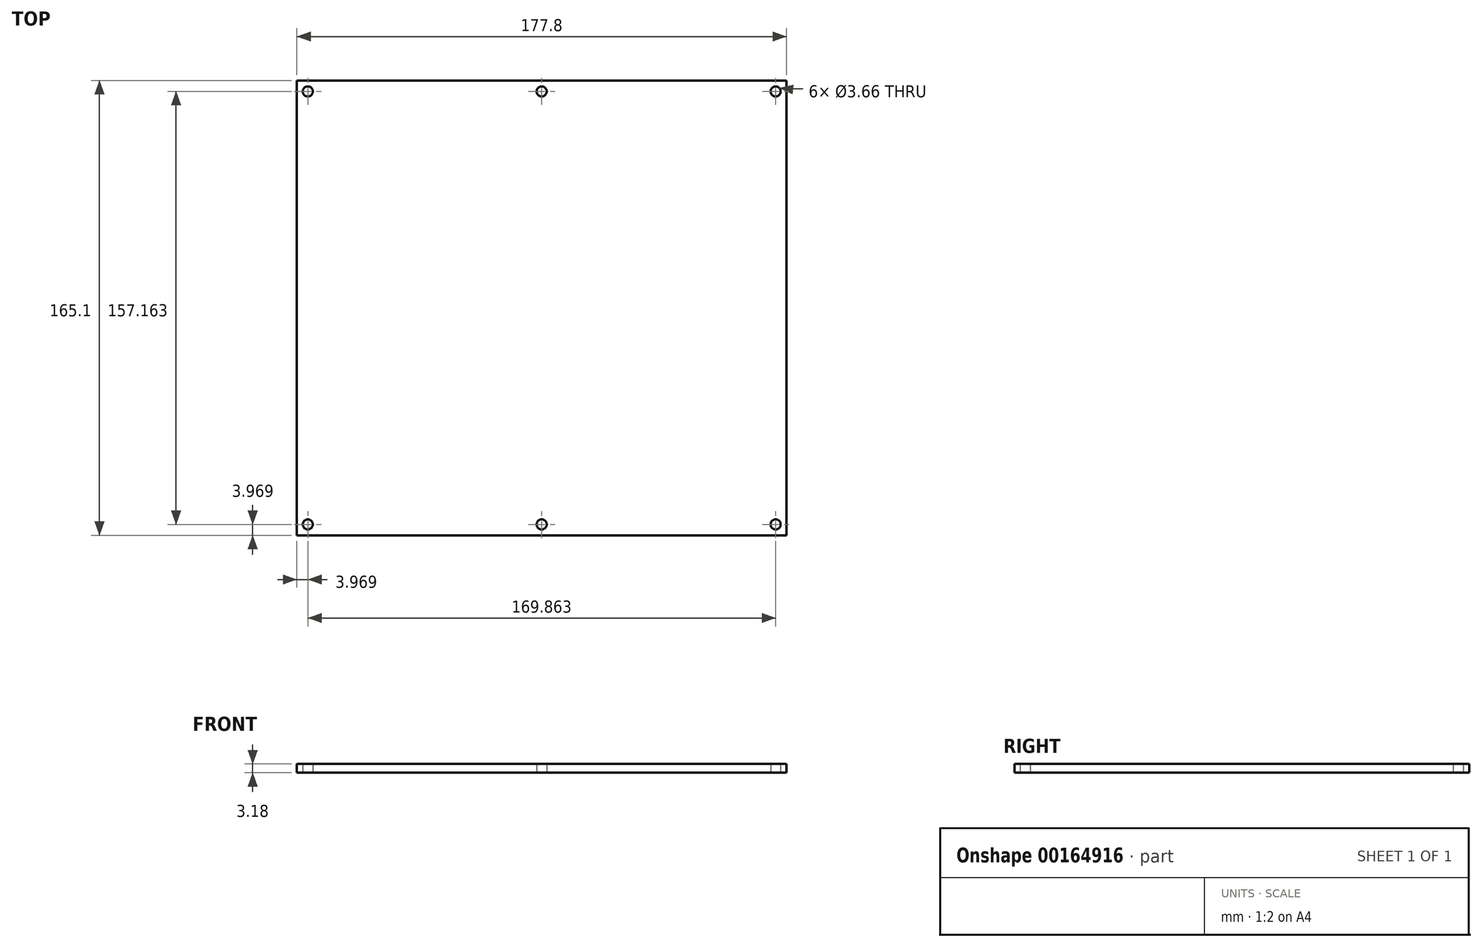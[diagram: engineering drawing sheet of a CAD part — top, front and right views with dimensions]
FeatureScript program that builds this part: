
annotation { "Feature Type Name" : "Feature", "Feature Type Description" : "" }
export const myFeature = defineFeature(function(context is Context, id is Id, definition is map)
    precondition{}
    {
        {
            var Q0;
            Q0=qCreatedBy(makeId("Top.planeOp"),FACE);
            var sketch = newSketch(context, id + "F0", { "sketchPlane" : qUnion([Q0])});
            skLineSegment(sketch, "E0.bottom", {"start": v(-88.9, 82.55) * mm, "end": v(88.9, 82.55) * mm});
            skLineSegment(sketch, "E0.top", {"start": v(-88.9, -82.55) * mm, "end": v(88.9, -82.55) * mm});
            skLineSegment(sketch, "E0.left", {"start": v(-88.9, 82.55) * mm, "end": v(-88.9, -82.55) * mm});
            skLineSegment(sketch, "E0.right", {"start": v(88.9, 82.55) * mm, "end": v(88.9, -82.55) * mm});
            skPoint(sketch, "E0.middle", {"position": v(0, 0) * mm});
            skLineSegment(sketch, "E1.bottom", {"start": v(-84.93, 78.58) * mm, "end": v(84.93, 78.58) * mm, "construction": true});
            skLineSegment(sketch, "E1.top", {"start": v(-84.93, -78.58) * mm, "end": v(84.93, -78.58) * mm, "construction": true});
            skLineSegment(sketch, "E1.left", {"start": v(-84.93, 78.58) * mm, "end": v(-84.93, -78.58) * mm, "construction": true});
            skLineSegment(sketch, "E1.right", {"start": v(84.93, 78.58) * mm, "end": v(84.93, -78.58) * mm, "construction": true});
            skLineSegment(sketch, "E2", {"start": v(-84.93, 78.58) * mm, "end": v(-88.9, 78.58) * mm, "construction": true});
            skLineSegment(sketch, "E3", {"start": v(-84.93, 78.58) * mm, "end": v(-84.93, 82.55) * mm, "construction": true});
            skCircle(sketch, "E4", {"center": v(84.93, -78.58) * mm, "radius": 1.83 * mm});
            skCircle(sketch, "E5", {"center": v(0, -78.58) * mm, "radius": 1.83 * mm});
            skCircle(sketch, "E6", {"center": v(-84.93, -78.58) * mm, "radius": 1.83 * mm});
            skCircle(sketch, "E7", {"center": v(-84.93, 78.58) * mm, "radius": 1.83 * mm});
            skCircle(sketch, "E8", {"center": v(0, 78.58) * mm, "radius": 1.83 * mm});
            skCircle(sketch, "E9", {"center": v(84.93, 78.58) * mm, "radius": 1.83 * mm});
            skSolve(sketch);
        }
        {
            var Q0;
            Q0 = qSketchRegion(id + "F0", true);
            extrude(context, id + "F1", {"entities" : qUnion([Q0]), "depth" : 3.17 * mm});
        }
    });
